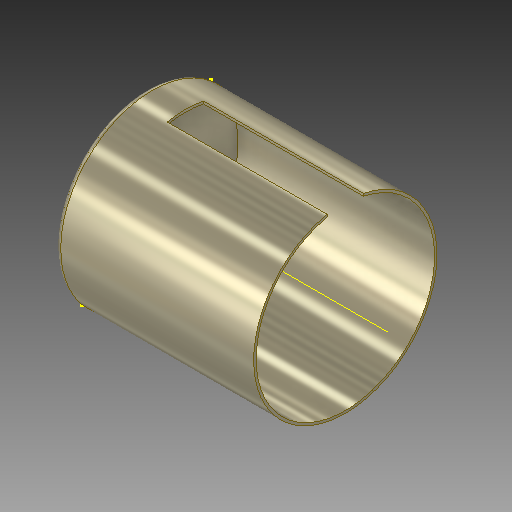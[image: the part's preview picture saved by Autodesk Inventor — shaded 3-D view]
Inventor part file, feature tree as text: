
AUTODESK INVENTOR PART (.ipt)
format: ipt  version: 2017.3 (Build 213256000, 256)  size: 239,616 bytes
history: native  units: mm
features: sketch x16, plane x10, extrude x9, fillet x1, other x1, hole x1
ambient origin geometry x8: Origin, YZ Plane, XZ Plane, XY Plane, X Axis, Y Axis, Z Axis, Center Point
bodies: Solid1 (feature_tree)
feature tree (38):
  extrude  "Extrusion1"  Depth=65.8mm TaperAngle=0.0deg
  extrude  "Extrusion2"  Depth=65.0mm TaperAngle=0.0deg
  fillet  "Fillet1"  Radius=2.0mm
  extrude  "Extrusion3"  Depth=5.0mm TaperAngle=0.0deg
  other  "Work Axis1"
  plane  "Work Plane2"
  plane  "Work Plane4"
  sketch  "Sketch4"  dims[d10=30.3mm d11=-60.6mm d12=30.3mm d13=-60.6mm]
  sketch  "Sketch5"  dims[d14=40.0mm d15=10.0mm]
  sketch  "Sketch6"  dims[d16=40.0mm d17=10.0mm d18=40.0mm d19=10.0mm]
  sketch  "Sketch7"  dims[d20=40.0mm d21=10.0mm d22=5.0mm d23=0.0mm]
  sketch  "Sketch8"  dims[d24=5.0mm d25=0.0mm d26=5.0mm d27=0.0mm]
  sketch  "Sketch9"  dims[d28=5.0mm d29=0.0mm]
  sketch  "Sketch10"  dims[d30=45.0deg d31=90.0deg d32=-30.3mm d33=30.3mm d34=-30.3mm d35=30.3mm d78=1.0mm d79=0.0mm]
  extrude  "Extrusion4"  Depth=30.3mm
  extrude  "Extrusion5"  Depth=10.0mm
  extrude  "Extrusion6"  Depth=10.0mm
  extrude  "Extrusion7"  Depth=10.0mm TaperAngle=0.0deg
  plane  "Work Plane5"
  plane  "Work Plane6"
  plane  "Work Plane7"
  plane  "Work Plane8"
  plane  "Work Plane9"
  plane  "Work Plane10"
  sketch  "Sketch11"  dims[d80=1.0mm d81=0.0mm]
  sketch  "Sketch12"  dims[d82=2.0mm d83=6.0mm d84=4.0mm d85=2.0mm d86=90.0deg d87=8.0mm d88=20.594885mm d36=1.0mm]
  sketch  "Sketch13"  dims[d37=1.0mm]
  sketch  "Sketch15"
  extrude  "Extrusion8"  Depth=5.0mm TaperAngle=0.0deg
  extrude  "Extrusion9"  Depth=1.0mm TaperAngle=0.0deg
  hole  "Hole7"  [1 undecoded]
  sketch  "Sketch1"  dims[d0=60.6mm d1=65.8mm d2=0.0mm]
  sketch  "Sketch2"  dims[d3=59.0mm d4=65.0mm d5=0.0mm d6=2.0mm]
  sketch  "Sketch3"  dims[d7=1.5mm d8=5.0mm d9=0.0mm]
  plane  "Work Plane1"
  plane  "Work Plane3"
  sketch  "Sketch17"
  sketch  "Sketch18"
note: 1 required parameter value undecoded (feature->parameter linkage not recoverable at this tier; creation-order binding heuristic only, values carry confidence <= 0.55)
